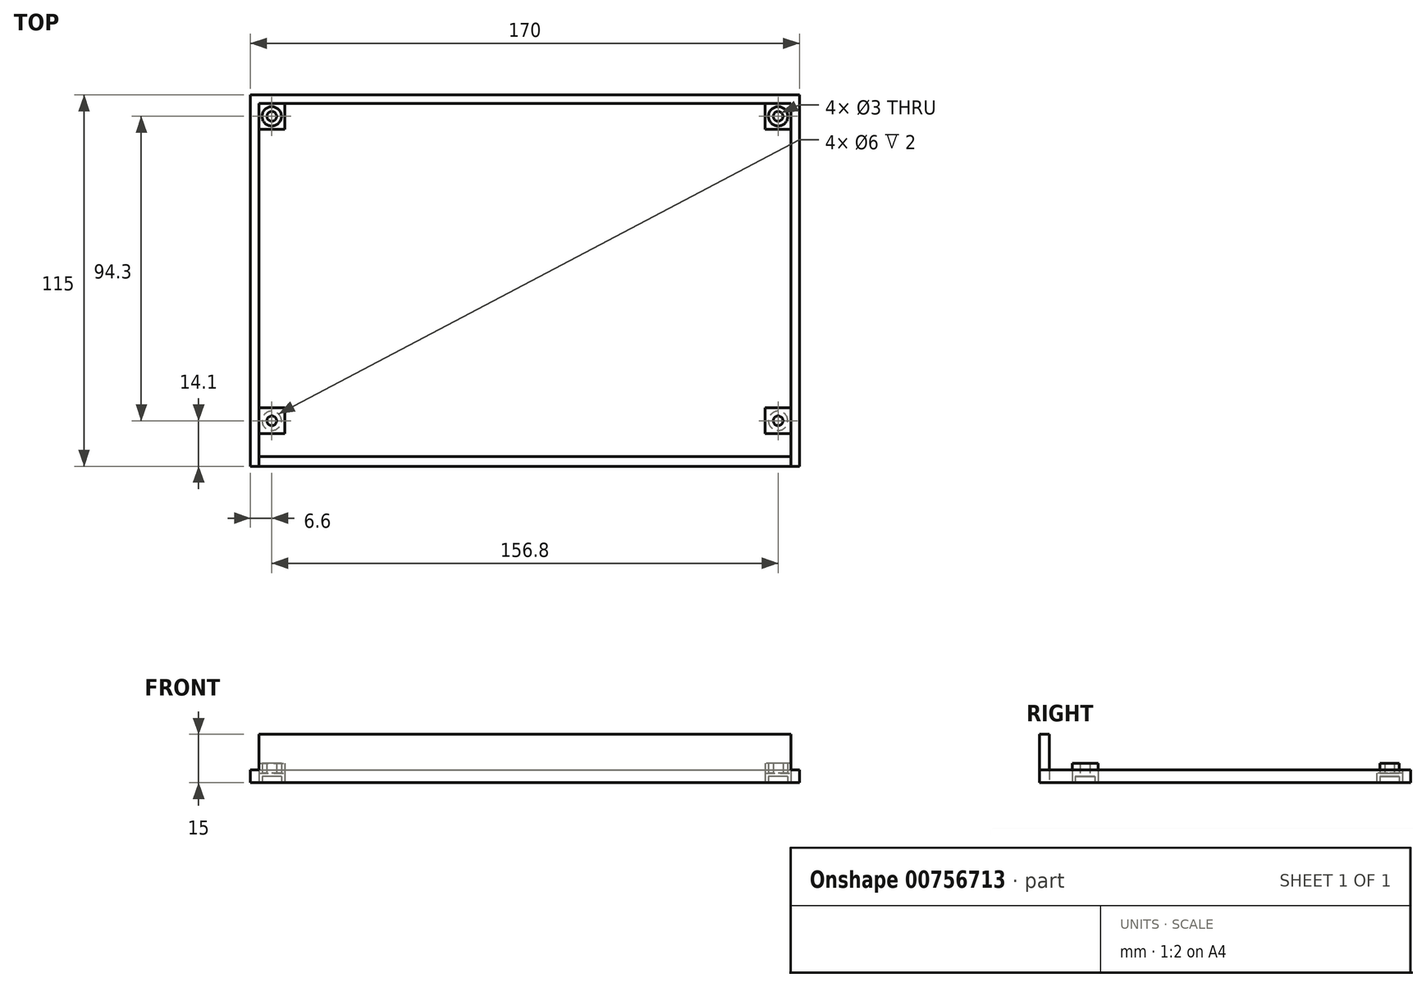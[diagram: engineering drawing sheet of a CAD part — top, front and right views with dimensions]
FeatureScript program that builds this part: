
annotation { "Feature Type Name" : "Feature", "Feature Type Description" : "" }
export const myFeature = defineFeature(function(context is Context, id is Id, definition is map)
    precondition{}
    {
        {
            var Q0;
            Q0=qCreatedBy(makeId("Top.planeOp"),FACE);
            var sketch = newSketch(context, id + "F0", { "sketchPlane" : qUnion([Q0])});
            skLineSegment(sketch, "E0.bottom", {"start": v(0, 0) * mm, "end": v(170, 0) * mm});
            skLineSegment(sketch, "E0.top", {"start": v(0, -115) * mm, "end": v(170, -115) * mm});
            skLineSegment(sketch, "E0.left", {"start": v(0, 0) * mm, "end": v(0, -115) * mm});
            skLineSegment(sketch, "E0.right", {"start": v(170, 0) * mm, "end": v(170, -115) * mm});
            skLineSegment(sketch, "E1", {"start": v(2.6, -115) * mm, "end": v(2.6, -2.6) * mm});
            skLineSegment(sketch, "E2", {"start": v(2.6, -2.6) * mm, "end": v(167.4, -2.6) * mm});
            skLineSegment(sketch, "E3", {"start": v(167.4, -2.6) * mm, "end": v(167.4, -115) * mm});
            skLineSegment(sketch, "E4", {"start": v(0, -67.06) * mm, "end": v(2.6, -67.06) * mm, "construction": true});
            skLineSegment(sketch, "E5", {"start": v(77.9, -2.6) * mm, "end": v(77.9, 0) * mm, "construction": true});
            skLineSegment(sketch, "E6", {"start": v(167.4, -63.68) * mm, "end": v(170, -63.68) * mm, "construction": true});
            skLineSegment(sketch, "E7.bottom", {"start": v(2.6, -2.6) * mm, "end": v(10.6, -2.6) * mm});
            skLineSegment(sketch, "E7.top", {"start": v(2.6, -10.6) * mm, "end": v(10.6, -10.6) * mm});
            skLineSegment(sketch, "E7.left", {"start": v(2.6, -2.6) * mm, "end": v(2.6, -10.6) * mm});
            skLineSegment(sketch, "E7.right", {"start": v(10.6, -2.6) * mm, "end": v(10.6, -10.6) * mm});
            skLineSegment(sketch, "E8.bottom", {"start": v(167.4, -2.6) * mm, "end": v(159.4, -2.6) * mm});
            skLineSegment(sketch, "E8.top", {"start": v(167.4, -10.6) * mm, "end": v(159.4, -10.6) * mm});
            skLineSegment(sketch, "E8.left", {"start": v(167.4, -2.6) * mm, "end": v(167.4, -10.6) * mm});
            skLineSegment(sketch, "E8.right", {"start": v(159.4, -2.6) * mm, "end": v(159.4, -10.6) * mm});
            skLineSegment(sketch, "E9.bottom", {"start": v(167.4, -96.9) * mm, "end": v(159.4, -96.9) * mm});
            skLineSegment(sketch, "E9.top", {"start": v(167.4, -104.9) * mm, "end": v(159.4, -104.9) * mm});
            skLineSegment(sketch, "E9.left", {"start": v(167.4, -96.9) * mm, "end": v(167.4, -104.9) * mm});
            skLineSegment(sketch, "E9.right", {"start": v(159.4, -96.9) * mm, "end": v(159.4, -104.9) * mm});
            skLineSegment(sketch, "E10.bottom", {"start": v(2.6, -96.9) * mm, "end": v(10.6, -96.9) * mm});
            skLineSegment(sketch, "E10.top", {"start": v(2.6, -104.9) * mm, "end": v(10.6, -104.9) * mm});
            skLineSegment(sketch, "E10.left", {"start": v(2.6, -96.9) * mm, "end": v(2.6, -104.9) * mm});
            skLineSegment(sketch, "E10.right", {"start": v(10.6, -96.9) * mm, "end": v(10.6, -104.9) * mm});
            skLineSegment(sketch, "E11", {"start": v(2.6, -112) * mm, "end": v(167.4, -112) * mm});
            skLineSegment(sketch, "E12", {"start": v(167.4, -112) * mm, "end": v(167.4, -115) * mm});
            skLineSegment(sketch, "E13", {"start": v(2.6, -115) * mm, "end": v(2.6, -112) * mm});
            skLineSegment(sketch, "E14", {"start": v(2.6, -2.6) * mm, "end": v(10.6, -10.6) * mm, "construction": true});
            skLineSegment(sketch, "E15", {"start": v(159.4, -2.6) * mm, "end": v(167.4, -10.6) * mm, "construction": true});
            skLineSegment(sketch, "E16", {"start": v(159.4, -96.9) * mm, "end": v(167.4, -104.9) * mm, "construction": true});
            skLineSegment(sketch, "E17", {"start": v(2.6, -96.9) * mm, "end": v(10.6, -104.9) * mm, "construction": true});
            skCircle(sketch, "E18", {"center": v(6.6, -6.6) * mm, "radius": 1.5 * mm});
            skCircle(sketch, "E19", {"center": v(163.4, -6.6) * mm, "radius": 1.5 * mm});
            skCircle(sketch, "E20", {"center": v(163.4, -100.9) * mm, "radius": 1.5 * mm});
            skCircle(sketch, "E21", {"center": v(6.6, -100.9) * mm, "radius": 1.5 * mm});
            skCircle(sketch, "E22", {"center": v(163.4, -6.6) * mm, "radius": 3 * mm});
            skCircle(sketch, "E23", {"center": v(6.6, -6.6) * mm, "radius": 3 * mm});
            skCircle(sketch, "E24", {"center": v(6.6, -100.9) * mm, "radius": 3 * mm});
            skCircle(sketch, "E25", {"center": v(163.4, -100.9) * mm, "radius": 3 * mm});
            skSolve(sketch);
        }
        {
            var Q0;
            Q0=makeQuery(id+"F0.imprint","IMPRINT",FACE,{"disambiguationData":[TD([[makeQuery(id+"F0.imprint","IMPRINT",EDGE,{"derivedFrom":sQuery(id+"F0.wireOp",EDGE,"E0.bottom")}),-1.0]])]});
            extrude(context, id + "F1", {"entities" : qUnion([Q0]), "depth" : 4 * mm, "offsetDistance" : 25 * mm});
        }
        {
            var Q0;
            Q0=makeQuery(id+"F0.imprint","IMPRINT",FACE,{"disambiguationData":[TD([[makeQuery(id+"F0.imprint","IMPRINT",EDGE,{"derivedFrom":sQuery(id+"F0.wireOp",EDGE,"E2")}),-1.0]])]});
            extrude(context, id + "F2", {"entities" : qUnion([Q0]), "operationType" : NewBodyOperationType.ADD, "depth" : 3 * mm, "offsetDistance" : 25 * mm});
        }
        {
            var Q0;
            Q0=makeQuery(id+"F0.imprint","IMPRINT",FACE,{"disambiguationData":[TD([[makeQuery(id+"F0.imprint","IMPRINT",EDGE,{"derivedFrom":sQuery(id+"F0.wireOp",EDGE,"E10.bottom")}),-1.0]])]});
            var Q1;
            Q1=makeQuery(id+"F0.imprint","IMPRINT",FACE,{"disambiguationData":[TD([[makeQuery(id+"F0.imprint","IMPRINT",EDGE,{"derivedFrom":sQuery(id+"F0.wireOp",EDGE,"E21")}),-1.0]])]});
            var Q2;
            Q2=makeQuery(id+"F0.imprint","IMPRINT",FACE,{"disambiguationData":[TD([[makeQuery(id+"F0.imprint","IMPRINT",EDGE,{"derivedFrom":sQuery(id+"F0.wireOp",EDGE,"E9.bottom")}),1.0]])]});
            var Q3;
            Q3=makeQuery(id+"F0.imprint","IMPRINT",FACE,{"disambiguationData":[TD([[makeQuery(id+"F0.imprint","IMPRINT",EDGE,{"derivedFrom":sQuery(id+"F0.wireOp",EDGE,"E20")}),-1.0]])]});
            var Q4;
            Q4=makeQuery(id+"F0.imprint","IMPRINT",FACE,{"disambiguationData":[TD([[makeQuery(id+"F0.imprint","IMPRINT",EDGE,{"derivedFrom":sQuery(id+"F0.wireOp",EDGE,"E8.bottom")}),1.0]])]});
            var Q5;
            Q5=makeQuery(id+"F0.imprint","IMPRINT",FACE,{"disambiguationData":[TD([[makeQuery(id+"F0.imprint","IMPRINT",EDGE,{"derivedFrom":sQuery(id+"F0.wireOp",EDGE,"E19")}),-1.0]])]});
            var Q6;
            Q6=makeQuery(id+"F0.imprint","IMPRINT",FACE,{"disambiguationData":[TD([[makeQuery(id+"F0.imprint","IMPRINT",EDGE,{"derivedFrom":sQuery(id+"F0.wireOp",EDGE,"E7.bottom")}),-1.0]])]});
            var Q7;
            Q7=makeQuery(id+"F0.imprint","IMPRINT",FACE,{"disambiguationData":[TD([[makeQuery(id+"F0.imprint","IMPRINT",EDGE,{"derivedFrom":sQuery(id+"F0.wireOp",EDGE,"E18")}),-1.0]])]});
            extrude(context, id + "F3", {"entities" : qUnion([Q0, Q1, Q2, Q3, Q4, Q5, Q6, Q7]), "operationType" : NewBodyOperationType.ADD, "depth" : 6 * mm, "offsetDistance" : 25 * mm});
        }
        {
            var Q0;
            Q0=makeQuery(id+"F0.imprint","IMPRINT",FACE,{"disambiguationData":[TD([[makeQuery(id+"F0.imprint","IMPRINT",EDGE,{"derivedFrom":sQuery(id+"F0.wireOp",EDGE,"E11")}),-1.0]])]});
            extrude(context, id + "F4", {"entities" : qUnion([Q0]), "operationType" : NewBodyOperationType.ADD, "depth" : 15 * mm, "offsetDistance" : 25 * mm});
        }
        {
            var Q0;
            Q0=makeQuery(id+"F0.imprint","IMPRINT",FACE,{"disambiguationData":[TD([[makeQuery(id+"F0.imprint","IMPRINT",EDGE,{"derivedFrom":sQuery(id+"F0.wireOp",EDGE,"E19")}),-1.0]])]});
            var Q1;
            Q1=makeQuery(id+"F0.imprint","IMPRINT",FACE,{"disambiguationData":[TD([[makeQuery(id+"F0.imprint","IMPRINT",EDGE,{"derivedFrom":sQuery(id+"F0.wireOp",EDGE,"E18")}),-1.0]])]});
            var Q2;
            Q2=makeQuery(id+"F0.imprint","IMPRINT",FACE,{"disambiguationData":[TD([[makeQuery(id+"F0.imprint","IMPRINT",EDGE,{"derivedFrom":sQuery(id+"F0.wireOp",EDGE,"E21")}),-1.0]])]});
            var Q3;
            Q3=makeQuery(id+"F0.imprint","IMPRINT",FACE,{"disambiguationData":[TD([[makeQuery(id+"F0.imprint","IMPRINT",EDGE,{"derivedFrom":sQuery(id+"F0.wireOp",EDGE,"E20")}),-1.0]])]});
            extrude(context, id + "F5", {"entities" : qUnion([Q0, Q1, Q2, Q3]), "operationType" : NewBodyOperationType.REMOVE, "depth" : 2 * mm, "offsetDistance" : 25 * mm});
        }
        {
            var Q0;
            {var subQ0=sQuery(id+"F0.wireOp",EDGE,"E13");var subQ1=sQuery(id+"F0.wireOp",EDGE,"E12");var subQ2=sQuery(id+"F0.wireOp",EDGE,"E11");var subQ3=sQuery(id+"F0.wireOp",EDGE,"E0.top");var subQ4=sQuery(id+"F0.wireOp",EDGE,"E10.right");var subQ5=sQuery(id+"F0.wireOp",EDGE,"E10.left");var subQ6=sQuery(id+"F0.wireOp",EDGE,"E10.top");var subQ7=sQuery(id+"F0.wireOp",EDGE,"E10.bottom");var subQ8=sQuery(id+"F0.wireOp",EDGE,"E9.right");var subQ9=sQuery(id+"F0.wireOp",EDGE,"E9.left");var subQ10=sQuery(id+"F0.wireOp",EDGE,"E9.top");var subQ11=sQuery(id+"F0.wireOp",EDGE,"E9.bottom");var subQ12=sQuery(id+"F0.wireOp",EDGE,"E8.right");var subQ13=sQuery(id+"F0.wireOp",EDGE,"E8.left");var subQ14=sQuery(id+"F0.wireOp",EDGE,"E8.top");var subQ15=sQuery(id+"F0.wireOp",EDGE,"E8.bottom");var subQ16=sQuery(id+"F0.wireOp",EDGE,"E7.right");var subQ17=sQuery(id+"F0.wireOp",EDGE,"E7.left");var subQ18=sQuery(id+"F0.wireOp",EDGE,"E7.top");var subQ19=sQuery(id+"F0.wireOp",EDGE,"E7.bottom");var subQ20=sQuery(id+"F0.wireOp",EDGE,"E3");var subQ21=sQuery(id+"F0.wireOp",EDGE,"E2");var subQ22=sQuery(id+"F0.wireOp",EDGE,"E1");Q0=makeQuery(id+"F4.boolean.opBoolean","MERGE",FACE,{"derivedFrom":[makeQuery(id+"F3.boolean.opBoolean","MERGE",FACE,{"derivedFrom":[makeQuery(id+"F2.boolean.opBoolean","MERGE",FACE,{"derivedFrom":[makeQuery(id+"F1.opExtrude","CAP_FACE",FACE,{"disambiguationData":[OSD([sQuery(id+"F0.wireOp",EDGE,"E0.bottom"),subQ3,sQuery(id+"F0.wireOp",EDGE,"E0.left"),sQuery(id+"F0.wireOp",EDGE,"E0.right"),subQ22,subQ21,subQ20,subQ19,subQ17,subQ15,subQ13,subQ9,subQ5,subQ1,subQ0])],"isStart":true}),makeQuery(id+"F2.opExtrude","CAP_FACE",FACE,{"disambiguationData":[OSD([subQ22,subQ21,subQ20,subQ18,subQ16,subQ14,subQ12,subQ11,subQ10,subQ8,subQ7,subQ6,subQ4,subQ2])],"isStart":true})]}),makeQuery(id+"F3.opExtrude","CAP_FACE",FACE,{"disambiguationData":[OSD([subQ19,subQ18,subQ17,subQ16,sQuery(id+"F0.wireOp",EDGE,"E18")])],"isStart":true}),makeQuery(id+"F3.opExtrude","CAP_FACE",FACE,{"disambiguationData":[OSD([subQ15,subQ14,subQ13,subQ12,sQuery(id+"F0.wireOp",EDGE,"E19")])],"isStart":true}),makeQuery(id+"F3.opExtrude","CAP_FACE",FACE,{"disambiguationData":[OSD([subQ11,subQ10,subQ9,subQ8,sQuery(id+"F0.wireOp",EDGE,"E20")])],"isStart":true}),makeQuery(id+"F3.opExtrude","CAP_FACE",FACE,{"disambiguationData":[OSD([subQ7,subQ6,subQ5,subQ4,sQuery(id+"F0.wireOp",EDGE,"E21")])],"isStart":true})]}),makeQuery(id+"F4.opExtrude","CAP_FACE",FACE,{"disambiguationData":[OSD([subQ3,subQ2,subQ1,subQ0])],"isStart":true})]});}
            var sketch = newSketch(context, id + "F6", { "sketchPlane" : qUnion([Q0])});
            skText(sketch, "E26", { "text": "Growth Box\n", "fontName": "AllertaStencil-Regular.ttf"});
            skLineSegment(sketch, "E27", {"start": v(144, 0) * mm, "end": v(144, 21.6) * mm, "construction": true});
            skLineSegment(sketch, "E28", {"start": v(144, 50) * mm, "end": v(26, 50) * mm, "construction": true});
            skLineSegment(sketch, "E29", {"start": v(26, 0) * mm, "end": v(26, 21.6) * mm, "construction": true});
            skLineSegment(sketch, "E30", {"start": v(144, 21.6) * mm, "end": v(170, 21.6) * mm, "construction": true});
            skLineSegment(sketch, "E31", {"start": v(26, 21.6) * mm, "end": v(0, 21.6) * mm, "construction": true});
            skText(sketch, "E32", { "text": "Controller", "fontName": "AllertaStencil-Regular.ttf"});
            skLineSegment(sketch, "E33", {"start": v(144, 75) * mm, "end": v(26, 75) * mm, "construction": true});
            skPoint(sketch, "E34", {"position": v(85, 75) * mm});
            skLineSegment(sketch, "E35", {"start": v(144, 95) * mm, "end": v(26, 95) * mm, "construction": true});
            skText(sketch, "E36", { "text": "By Marcus, Rasmus \n& Soeren", "fontName": "AllertaStencil-Regular.ttf"});
            skPoint(sketch, "E37", {"position": v(84.76, 95) * mm});
            skLineSegment(sketch, "E38", {"start": v(26, 85.9) * mm, "end": v(0, 85.9) * mm, "construction": true});
            skLineSegment(sketch, "E39", {"start": v(144, 85.9) * mm, "end": v(170, 85.9) * mm, "construction": true});
            skLineSegment(sketch, "E40", {"start": v(163.4, 100.9) * mm, "end": v(163.4, 85.9) * mm, "construction": true});
            skLineSegment(sketch, "E41", {"start": v(6.6, 100.9) * mm, "end": v(6.6, 85.9) * mm, "construction": true});
            skLineSegment(sketch, "E42", {"start": v(6.6, 6.6) * mm, "end": v(6.6, 21.6) * mm, "construction": true});
            skLineSegment(sketch, "E43", {"start": v(163.4, 6.6) * mm, "end": v(163.4, 21.6) * mm, "construction": true});
            skLineSegment(sketch, "E44", {"start": v(26, 50) * mm, "end": v(144, 50) * mm});
            skLineSegment(sketch, "E45.trimOffspring", {"start": v(144, 75) * mm, "end": v(144, 115) * mm, "construction": true});
            skLineSegment(sketch, "E46.trimOffspring", {"start": v(26, 75) * mm, "end": v(26, 115) * mm, "construction": true});
            skPoint(sketch, "E47.start.orphan", {"position": v(26, 52) * mm});
            skText(sketch, "E48", { "text": "Growth-In-A-Box", "fontName": "AllertaStencil-Regular.ttf"});
            const initialGuessF6  = {"E26": [0.144, 0.05, -1, 0, 0.01436], "E32": [0.1275, 0.075, -1, 0, 0.0117], "E36": [0.144, 0.095, -1, 0, 0.009], "E48": [0.144, 0.0216, -1, 0, 0.00972]};
            skSetInitialGuess(sketch, initialGuessF6);
            skSolve(sketch);
        }
        {
            var Q0;
            Q0 = qSketchRegion(id + "F6", true);
            extrude(context, id + "F7", {"entities" : qUnion([Q0]), "operationType" : NewBodyOperationType.REMOVE, "oppositeDirection" : true, "depth" : 25 * mm, "offsetDistance" : 25 * mm});
        }
    });
